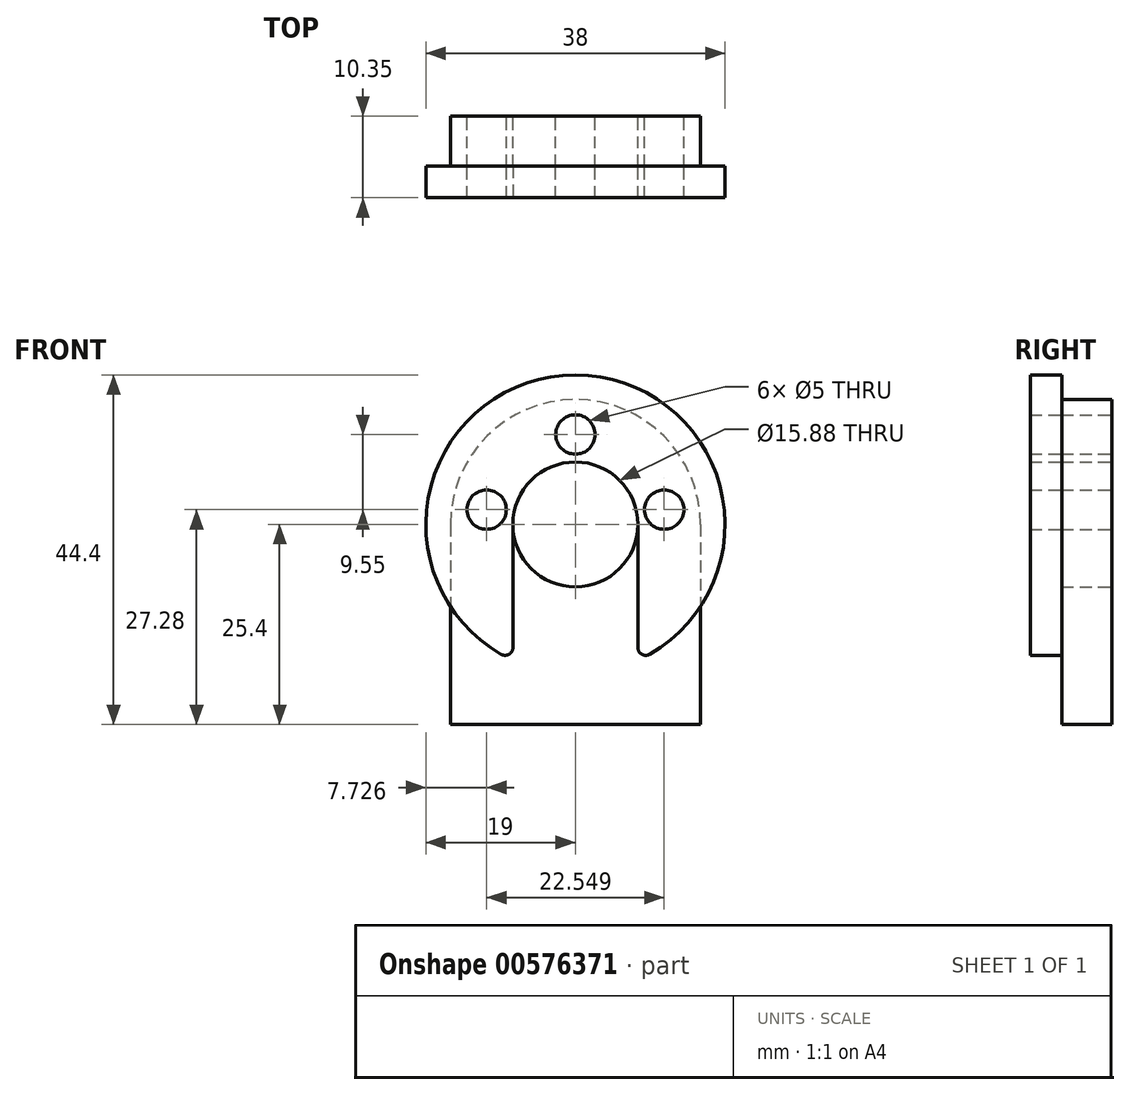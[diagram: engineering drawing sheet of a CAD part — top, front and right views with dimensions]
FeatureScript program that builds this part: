
annotation { "Feature Type Name" : "Feature", "Feature Type Description" : "" }
export const myFeature = defineFeature(function(context is Context, id is Id, definition is map)
    precondition{}
    {
        {
            var Q0;
            Q0=qCreatedBy(makeId("Front.planeOp"),FACE);
            var sketch = newSketch(context, id + "F0", { "sketchPlane" : qUnion([Q0]), "asVersion" : FeatureScriptVersionNumber.V686_LOFT_FS_BUG_FIXES});
            skCircle(sketch, "E0", {"center": v(0, 0) * mm, "radius": 7.94 * mm});
            skArc(sketch, "E1", {"start": v(15.88, 0) * mm, "mid": v(0, 15.88) * mm, "end": v(-15.88, 0) * mm});
            skLineSegment(sketch, "E2", {"start": v(15.88, 0) * mm, "end": v(15.88, -25.4) * mm});
            skLineSegment(sketch, "E3", {"start": v(-15.88, 0) * mm, "end": v(-15.88, -25.4) * mm});
            skLineSegment(sketch, "E4", {"start": v(-15.88, -25.4) * mm, "end": v(15.88, -25.4) * mm});
            skCircle(sketch, "E5", {"center": v(11.27, 1.88) * mm, "radius": 2.5 * mm});
            skCircle(sketch, "E6", {"center": v(0, 11.43) * mm, "radius": 2.5 * mm});
            skCircle(sketch, "E7", {"center": v(-11.27, 1.88) * mm, "radius": 2.5 * mm});
            skLineSegment(sketch, "E8", {"start": v(0, 18.27) * mm, "end": v(0, -28.72) * mm, "construction": true});
            skLineSegment(sketch, "E9", {"start": v(18.17, 1.88) * mm, "end": v(-18.68, 1.88) * mm, "construction": true});
            skCircle(sketch, "E10", {"center": v(0, 0) * mm, "radius": 11.43 * mm, "construction": true});
            skPoint(sketch, "E11", {"position": v(0, 13.93) * mm});
            skPoint(sketch, "E12", {"position": v(0, 15.88) * mm});
            skSolve(sketch);
        }
        {
            var Q0;
            Q0 = qSketchRegion(id + "F0", true);
            extrude(context, id + "F1", {"entities" : qUnion([Q0]), "depth" : 6.35 * mm, "offsetDistance" : 25 * mm});
        }
        {
            var Q0;
            Q0=makeQuery(id+"F1.opExtrude","CAP_FACE",FACE,{"disambiguationData":[OSD([sQuery(id+"F0.wireOp",EDGE,"E0"),sQuery(id+"F0.wireOp",EDGE,"E1"),sQuery(id+"F0.wireOp",EDGE,"E2"),sQuery(id+"F0.wireOp",EDGE,"E3"),sQuery(id+"F0.wireOp",EDGE,"E4"),sQuery(id+"F0.wireOp",EDGE,"E5"),sQuery(id+"F0.wireOp",EDGE,"E6"),sQuery(id+"F0.wireOp",EDGE,"E7")])],"isStart":false});
            var sketch = newSketch(context, id + "F2", { "sketchPlane" : qUnion([Q0])});
            skCircle(sketch, "E13.0", {"center": v(-11.27, 1.88) * mm, "radius": 2.5 * mm});
            skCircle(sketch, "E14.0", {"center": v(0, 11.43) * mm, "radius": 2.5 * mm});
            skCircle(sketch, "E15.0", {"center": v(11.27, 1.88) * mm, "radius": 2.5 * mm});
            skArc(sketch, "E16.0", {"start": v(7.94, 0) * mm, "mid": v(0, 7.94) * mm, "end": v(-7.94, 0) * mm});
            skArc(sketch, "E17", {"start": v(7.94, -17.26) * mm, "mid": v(0, 19) * mm, "end": v(-7.94, -17.26) * mm});
            skLineSegment(sketch, "E18", {"start": v(-7.94, 0) * mm, "end": v(-7.94, -17.26) * mm});
            skLineSegment(sketch, "E19", {"start": v(7.94, 0) * mm, "end": v(7.94, -17.26) * mm});
            skSolve(sketch);
        }
        {
            var Q0;
            Q0 = qSketchRegion(id + "F2", true);
            extrude(context, id + "F3", {"entities" : qUnion([Q0]), "depth" : 4 * mm, "offsetDistance" : 25 * mm});
        }
        {
            var Q0;
            Q0=makeQuery(id+"F3.opExtrude","SWEPT_EDGE",EDGE,{"disambiguationData":[OSD([sQuery(id+"F2.wireOp",EDGE,"E17"),sQuery(id+"F2.wireOp",EDGE,"E19")])]});
            var Q1;
            Q1=makeQuery(id+"F3.opExtrude","SWEPT_EDGE",EDGE,{"disambiguationData":[OSD([sQuery(id+"F2.wireOp",EDGE,"E17"),sQuery(id+"F2.wireOp",EDGE,"E18")])]});
            fillet(context, id + "F4", {"entities" : qUnion([Q0, Q1]), "radius" : 1 * mm, "tangentPropagation" : true, "allowEdgeOverflow" : false});
        }
    });
